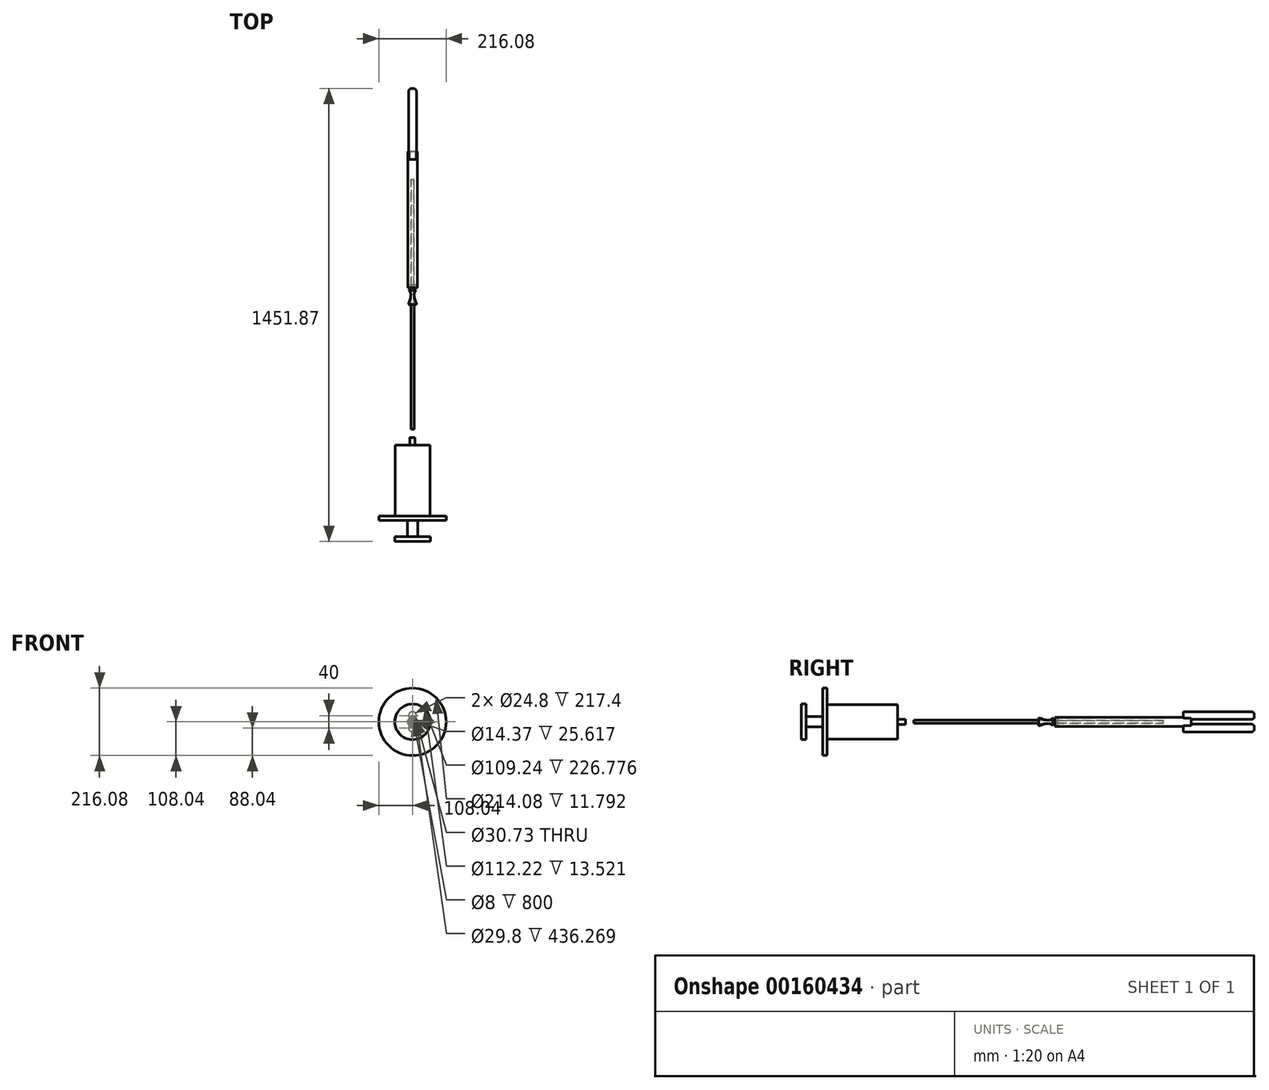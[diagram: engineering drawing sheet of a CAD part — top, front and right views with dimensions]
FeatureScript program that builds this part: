
annotation { "Feature Type Name" : "Feature", "Feature Type Description" : "" }
export const myFeature = defineFeature(function(context is Context, id is Id, definition is map)
    precondition{}
    {
        {
            var Q0;
            Q0=qCreatedBy(makeId("Top.planeOp"),FACE);
            var sketch = newSketch(context, id + "F0", { "sketchPlane" : qUnion([Q0])});
            skCircle(sketch, "E0", {"center": v(0, 0) * mm, "radius": 15 * mm});
            skSolve(sketch);
        }
        {
            var Q0;
            Q0=makeQuery(id+"F0.imprint","IMPRINT",FACE,{"disambiguationData":[TD([[makeQuery(id+"F0.imprint","IMPRINT",EDGE,{"derivedFrom":sQuery(id+"F0.wireOp",EDGE,"E0")}),1.0]])]});
            extrude(context, id + "F1", {"entities" : qUnion([Q0]), "endBound" : BoundingType.SYMMETRIC, "depth" : 400 * mm});
        }
        {
            var Q0;
            Q0=qCreatedBy(makeId("Front.planeOp"),FACE);
            var sketch = newSketch(context, id + "F2", { "sketchPlane" : qUnion([Q0])});
            skCircle(sketch, "E1", {"center": v(0, 0) * mm, "radius": 15 * mm});
            skSolve(sketch);
        }
        {
            var Q0;
            Q0=qSketchRegion(id+"F2",true);
            extrude(context, id + "F3", {"entities" : qUnion([Q0]), "operationType" : NewBodyOperationType.ADD, "depth" : 500 * mm});
        }
        {
            var Q0;
            Q0=makeQuery(id+"F1.opExtrude","CAP_EDGE",EDGE,{"disambiguationData":[OSD([sQuery(id+"F0.wireOp",EDGE,"E0")])],"isStart":false});
            var Q1;
            Q1=makeQuery(id+"F1.opExtrude","CAP_EDGE",EDGE,{"disambiguationData":[OSD([sQuery(id+"F0.wireOp",EDGE,"E0")])],"isStart":true});
            fillet(context, id + "F4", {"entities" : qUnion([Q0, Q1]), "radius" : 10 * mm, "tangentPropagation" : true, "allowEdgeOverflow" : false});
        }
        {
            var Q0;
            Q0=qCreatedBy(makeId("Right.planeOp"),FACE);
            var sketch = newSketch(context, id + "F5", { "sketchPlane" : qUnion([Q0])});
            skLineSegment(sketch, "E2.bottom", {"start": v(-59.18, 332.97) * mm, "end": v(118.79, 332.97) * mm});
            skLineSegment(sketch, "E2.top", {"start": v(-59.18, -401.27) * mm, "end": v(118.79, -401.27) * mm});
            skLineSegment(sketch, "E2.left", {"start": v(-59.18, 332.97) * mm, "end": v(-59.18, -401.27) * mm});
            skLineSegment(sketch, "E2.right", {"start": v(118.79, 332.97) * mm, "end": v(118.79, -401.27) * mm});
            skSolve(sketch);
        }
        {
            var Q0;
            Q0=makeQuery(id+"F5.imprint","IMPRINT",FACE,{"disambiguationData":[TD([[makeQuery(id+"F5.imprint","IMPRINT",EDGE,{"derivedFrom":sQuery(id+"F5.wireOp",EDGE,"E2.bottom")}),-1.0]])]});
            extrude(context, id + "F6", {"entities" : qUnion([Q0]), "operationType" : NewBodyOperationType.REMOVE, "endBound" : BoundingType.SYMMETRIC, "oppositeDirection" : true, "depth" : 40 * mm});
        }
        {
            var Q0;
            Q0=makeQuery(id+"F6.boolean.opBoolean","COPY",FACE,{"derivedFrom":makeQuery(id+"F6.opExtrude","SWEPT_FACE",FACE,{"disambiguationData":[OSD([sQuery(id+"F5.wireOp",EDGE,"E2.left")])]})});
            var sketch = newSketch(context, id + "F7", { "sketchPlane" : qUnion([Q0])});
            skLineSegment(sketch, "E3.0", {"start": v(0, 332.97) * mm, "end": v(0, -401.27) * mm, "construction": true});
            skCircle(sketch, "E4", {"center": v(0, -20) * mm, "radius": 12.5 * mm});
            skCircle(sketch, "E5", {"center": v(0, 20) * mm, "radius": 12.5 * mm});
            skSolve(sketch);
        }
        {
            var Q0;
            {var subQ0=sQuery(id+"F7.wireOp",EDGE,"E4");var subQ1=makeQuery(id+"F6.boolean.opBoolean","INTERSECT",EDGE,{"derivedFrom":[makeQuery(id+"F3.opExtrude","SWEPT_FACE",FACE,{"disambiguationData":[OSD([sQuery(id+"F2.wireOp",EDGE,"E1")])]}),makeQuery(id+"F6.opExtrude","SWEPT_FACE",FACE,{"disambiguationData":[OSD([sQuery(id+"F5.wireOp",EDGE,"E2.left")])]})]});var subQ2=makeQuery(id+"F7.imprint","INTERSECT",VERTEX,{"disambiguationData":[OD(0.0)],"derivedFrom":[subQ1,subQ0]});Q0=makeQuery(id+"F7.imprint","IMPRINT",FACE,{"disambiguationData":[TD([[makeQuery(id+"F7.imprint","IMPRINT",EDGE,{"disambiguationData":[TD([[subQ2,1.0]])],"derivedFrom":subQ0}),1.0]])]});}
            var Q1;
            {var subQ0=sQuery(id+"F7.wireOp",EDGE,"E4");var subQ1=makeQuery(id+"F7.imprint","INTERSECT",VERTEX,{"derivedFrom":[subQ0,sQuery(id+"F7.wireOp",EDGE,"E5")]});Q1=makeQuery(id+"F7.imprint","IMPRINT",FACE,{"disambiguationData":[TD([[makeQuery(id+"F7.imprint","IMPRINT",EDGE,{"disambiguationData":[TD([[subQ1,1.0]])],"derivedFrom":subQ0}),1.0]])]});}
            var Q2;
            {var subQ0=sQuery(id+"F7.wireOp",EDGE,"E5");var subQ1=makeQuery(id+"F7.imprint","INTERSECT",VERTEX,{"derivedFrom":[sQuery(id+"F7.wireOp",EDGE,"E4"),subQ0]});Q2=makeQuery(id+"F7.imprint","IMPRINT",FACE,{"disambiguationData":[TD([[makeQuery(id+"F7.imprint","IMPRINT",EDGE,{"disambiguationData":[TD([[subQ1,1.0]])],"derivedFrom":subQ0}),1.0]])]});}
            var Q3;
            {var subQ0=sQuery(id+"F7.wireOp",EDGE,"E5");var subQ1=makeQuery(id+"F6.boolean.opBoolean","INTERSECT",EDGE,{"derivedFrom":[makeQuery(id+"F3.opExtrude","SWEPT_FACE",FACE,{"disambiguationData":[OSD([sQuery(id+"F2.wireOp",EDGE,"E1")])]}),makeQuery(id+"F6.opExtrude","SWEPT_FACE",FACE,{"disambiguationData":[OSD([sQuery(id+"F5.wireOp",EDGE,"E2.left")])]})]});var subQ2=makeQuery(id+"F7.imprint","INTERSECT",VERTEX,{"disambiguationData":[OD(0.0)],"derivedFrom":[subQ1,subQ0]});Q3=makeQuery(id+"F7.imprint","IMPRINT",FACE,{"disambiguationData":[TD([[makeQuery(id+"F7.imprint","IMPRINT",EDGE,{"disambiguationData":[TD([[subQ2,1.0]])],"derivedFrom":subQ0}),1.0]])]});}
            extrude(context, id + "F8", {"entities" : qUnion([Q0, Q1, Q2, Q3]), "depth" : 202.5 * mm});
        }
        {
            var Q0;
            Q0=makeQuery(id+"F8.opExtrude","CAP_FACE",FACE,{"disambiguationData":[OSD([sQuery(id+"F7.wireOp",EDGE,"E5")])],"isStart":true});
            var Q1;
            Q1=makeQuery(id+"F8.opExtrude","CAP_FACE",FACE,{"disambiguationData":[OSD([sQuery(id+"F7.wireOp",EDGE,"E4")])],"isStart":true});
            extrude(context, id + "F9", {"entities" : qUnion([Q0, Q1]), "operationType" : NewBodyOperationType.ADD, "depth" : 25 * mm});
        }
        {
            var Q0;
            Q0=makeQuery(id+"F8.opExtrude","CAP_EDGE",EDGE,{"disambiguationData":[OSD([sQuery(id+"F7.wireOp",EDGE,"E4")])],"isStart":false});
            var Q1;
            Q1=makeQuery(id+"F8.opExtrude","CAP_EDGE",EDGE,{"disambiguationData":[OSD([sQuery(id+"F7.wireOp",EDGE,"E5")])],"isStart":false});
            fillet(context, id + "F10", {"entities" : qUnion([Q0, Q1]), "radius" : 10 * mm, "tangentPropagation" : true, "allowEdgeOverflow" : false});
        }
        {
            var Q0;
            Q0=qCreatedBy(makeId("Right.planeOp"),FACE);
            var sketch = newSketch(context, id + "F11", { "sketchPlane" : qUnion([Q0])});
            skLineSegment(sketch, "E6.0", {"start": v(-500, -15) * mm, "end": v(-500, 15) * mm});
            skFitSpline(sketch, "E7", {"points": [v(-500, -15) * mm, v(-524.47, -6) * mm, v(-560.23, -15) * mm, v(-560.23, 0) * mm], "startDerivative": vector(-59.25, 72.79) * mm, "endDerivative": vector(-9.37, 82.85) * mm});
            skLineSegment(sketch, "E8", {"start": v(-500, 0) * mm, "end": v(-548.33, 0) * mm, "construction": true});
            skPoint(sketch, "E8.endSnap0", {"position": v(-500, 0) * mm});
            skLineSegment(sketch, "E9", {"start": v(-548.33, 0) * mm, "end": v(-500, 0) * mm});
            skLineSegment(sketch, "E10", {"start": v(-548.33, -13.18) * mm, "end": v(-548.33, 0) * mm});
            skSolve(sketch);
        }
        {
            var Q0;
            {var subQ0=sQuery(id+"F11.wireOp",EDGE,"E7");Q0=makeQuery(id+"F11.imprint","IMPRINT",FACE,{"disambiguationData":[TD([[makeQuery(id+"F11.imprint","IMPRINT",EDGE,{"derivedFrom":subQ0}),-1.0]])]});}
            var Q1;
            Q1=sQuery(id+"F11.wireOp",EDGE,"E9");
            revolve(context, id + "F12", {"operationType" : NewBodyOperationType.ADD, "entities" : qUnion([Q0]), "axis" : qUnion([Q1]), "revolveType" : RevolveType.FULL});
        }
        {
            var Q0;
            Q0=makeQuery(id+"F12.boolean.opBoolean","MERGE",EDGE,{"derivedFrom":[makeQuery(id+"F3.opExtrude","CAP_EDGE",EDGE,{"disambiguationData":[OSD([sQuery(id+"F2.wireOp",EDGE,"E1")])],"isStart":false}),makeQuery(id+"F12.opRevolve","SWEPT_EDGE",EDGE,{"disambiguationData":[OSD([sQuery(id+"F11.wireOp",EDGE,"E6.0"),sQuery(id+"F11.wireOp",EDGE,"E7")])]})]});
            fillet(context, id + "F13", {"entities" : qUnion([Q0]), "radius" : 10 * mm, "tangentPropagation" : true, "allowEdgeOverflow" : false});
        }
        {
            var Q0;
            Q0=makeQuery(id+"F12.opRevolve","SWEPT_FACE",FACE,{"disambiguationData":[OSD([sQuery(id+"F11.wireOp",EDGE,"E10")])]});
            var sketch = newSketch(context, id + "F14", { "sketchPlane" : qUnion([Q0])});
            skCircle(sketch, "E11", {"center": v(0, 0) * mm, "radius": 5 * mm});
            skCircle(sketch, "E12", {"center": v(0, 0) * mm, "radius": 4 * mm});
            skSolve(sketch);
        }
        {
            var Q0;
            Q0=makeQuery(id+"F12.opRevolve","SWEPT_FACE",FACE,{"disambiguationData":[OSD([sQuery(id+"F11.wireOp",EDGE,"E10")])]});
            shell(context, id + "F15", {"entities" : qUnion([Q0]), "thickness" : 0.1 * mm});
        }
        {
            var Q0;
            Q0=makeQuery(id+"F14.imprint","IMPRINT",FACE,{"disambiguationData":[TD([[makeQuery(id+"F14.imprint","IMPRINT",EDGE,{"derivedFrom":sQuery(id+"F14.wireOp",EDGE,"E11")}),1.0]])]});
            extrude(context, id + "F16", {"entities" : qUnion([Q0]), "endBound" : BoundingType.SYMMETRIC, "depth" : 800 * mm});
        }
        {
            var Q0;
            Q0=qCreatedBy(makeId("Right.planeOp"),FACE);
            var sketch = newSketch(context, id + "F17", { "sketchPlane" : qUnion([Q0])});
            skLineSegment(sketch, "E13.0", {"start": v(-948.33, -5) * mm, "end": v(-948.33, 5) * mm});
            skLineSegment(sketch, "E14.bottom", {"start": v(-975.26, 0) * mm, "end": v(-999.88, 0) * mm});
            skLineSegment(sketch, "E14.top", {"start": v(-975.26, 8.18) * mm, "end": v(-999.88, 8.18) * mm});
            skLineSegment(sketch, "E14.left", {"start": v(-975.26, 0) * mm, "end": v(-975.26, 8.18) * mm});
            skLineSegment(sketch, "E14.right", {"start": v(-999.88, 0) * mm, "end": v(-999.88, 8.18) * mm});
            skLineSegment(sketch, "E15.bottom", {"start": v(-999.88, 0) * mm, "end": v(-1226.66, 0) * mm});
            skLineSegment(sketch, "E15.top", {"start": v(-999.88, 55.62) * mm, "end": v(-1226.66, 55.62) * mm});
            skLineSegment(sketch, "E15.left", {"start": v(-999.88, 0) * mm, "end": v(-999.88, 55.62) * mm});
            skLineSegment(sketch, "E15.right", {"start": v(-1226.66, 0) * mm, "end": v(-1226.66, 55.62) * mm});
            skLineSegment(sketch, "E16.bottom", {"start": v(-1226.66, 0) * mm, "end": v(-1240.45, 0) * mm});
            skLineSegment(sketch, "E16.top", {"start": v(-1226.66, 108.04) * mm, "end": v(-1240.45, 108.04) * mm});
            skLineSegment(sketch, "E16.left", {"start": v(-1226.66, 0) * mm, "end": v(-1226.66, 108.04) * mm});
            skLineSegment(sketch, "E16.right", {"start": v(-1240.45, 0) * mm, "end": v(-1240.45, 108.04) * mm});
            skLineSegment(sketch, "E17.bottom", {"start": v(-1240.45, 0) * mm, "end": v(-1293.03, 0) * mm});
            skLineSegment(sketch, "E17.top", {"start": v(-1240.45, 16.37) * mm, "end": v(-1293.03, 16.37) * mm});
            skLineSegment(sketch, "E17.left", {"start": v(-1240.45, 0) * mm, "end": v(-1240.45, 16.37) * mm});
            skLineSegment(sketch, "E17.right", {"start": v(-1293.03, 0) * mm, "end": v(-1293.03, 16.37) * mm});
            skLineSegment(sketch, "E18.bottom", {"start": v(-1293.03, 0) * mm, "end": v(-1308.55, 0) * mm});
            skLineSegment(sketch, "E18.top", {"start": v(-1293.03, 57.11) * mm, "end": v(-1308.55, 57.11) * mm});
            skLineSegment(sketch, "E18.left", {"start": v(-1293.03, 0) * mm, "end": v(-1293.03, 57.11) * mm});
            skLineSegment(sketch, "E18.right", {"start": v(-1308.55, 0) * mm, "end": v(-1308.55, 57.11) * mm});
            skSolve(sketch);
        }
        {
            var Q0;
            {var subQ1=sQuery(id+"F17.wireOp",EDGE,"E15.bottom");Q0=makeQuery(id+"F17.imprint","IMPRINT",FACE,{"disambiguationData":[TD([[makeQuery(id+"F17.imprint","IMPRINT",EDGE,{"derivedFrom":subQ1}),-1.0]])]});}
            var Q1;
            {var subQ0=sQuery(id+"F17.wireOp",EDGE,"E14.bottom");Q1=makeQuery(id+"F17.imprint","IMPRINT",FACE,{"disambiguationData":[TD([[makeQuery(id+"F17.imprint","IMPRINT",EDGE,{"derivedFrom":subQ0}),-1.0]])]});}
            var Q2;
            {var subQ0=sQuery(id+"F17.wireOp",EDGE,"E17.bottom");Q2=makeQuery(id+"F17.imprint","IMPRINT",FACE,{"disambiguationData":[TD([[makeQuery(id+"F17.imprint","IMPRINT",EDGE,{"derivedFrom":subQ0}),-1.0]])]});}
            var Q3;
            {var subQ1=sQuery(id+"F17.wireOp",EDGE,"E16.bottom");Q3=makeQuery(id+"F17.imprint","IMPRINT",FACE,{"disambiguationData":[TD([[makeQuery(id+"F17.imprint","IMPRINT",EDGE,{"derivedFrom":subQ1}),-1.0]])]});}
            var Q4;
            {var subQ3=sQuery(id+"F17.wireOp",EDGE,"E18.bottom");Q4=makeQuery(id+"F17.imprint","IMPRINT",FACE,{"disambiguationData":[TD([[makeQuery(id+"F17.imprint","IMPRINT",EDGE,{"derivedFrom":subQ3}),-1.0]])]});}
            var Q5;
            Q5=sQuery(id+"F17.wireOp",EDGE,"E15.bottom");
            revolve(context, id + "F18", {"entities" : qUnion([Q0, Q1, Q2, Q3, Q4]), "axis" : qUnion([Q5]), "revolveType" : RevolveType.FULL});
        }
        {
            var Q0;
            Q0=makeQuery(id+"F18.opRevolve","SWEPT_FACE",FACE,{"disambiguationData":[OSD([sQuery(id+"F17.wireOp",EDGE,"E14.left")])]});
            shell(context, id + "F19", {"entities" : qUnion([Q0]), "thickness" : 1 * mm});
        }
    });
